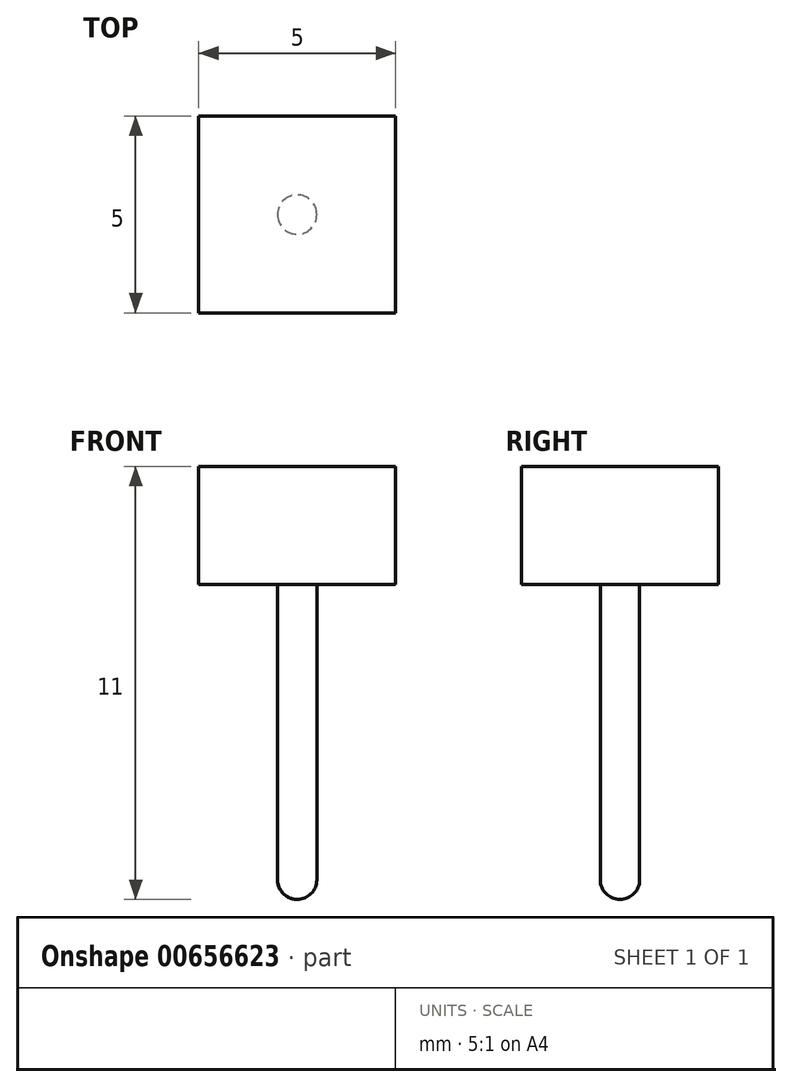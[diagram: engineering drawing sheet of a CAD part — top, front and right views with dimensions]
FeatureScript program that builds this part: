
annotation { "Feature Type Name" : "Feature", "Feature Type Description" : "" }
export const myFeature = defineFeature(function(context is Context, id is Id, definition is map)
    precondition{}
    {
        {
            var Q0;
            Q0=qCreatedBy(makeId("Top.planeOp"),FACE);
            var sketch = newSketch(context, id + "F0", { "sketchPlane" : qUnion([Q0])});
            skLineSegment(sketch, "E0.bottom", {"start": v(2.5, -2.5) * mm, "end": v(-2.5, -2.5) * mm});
            skLineSegment(sketch, "E0.top", {"start": v(2.5, 2.5) * mm, "end": v(-2.5, 2.5) * mm});
            skLineSegment(sketch, "E0.left", {"start": v(2.5, -2.5) * mm, "end": v(2.5, 2.5) * mm});
            skLineSegment(sketch, "E0.right", {"start": v(-2.5, -2.5) * mm, "end": v(-2.5, 2.5) * mm});
            skPoint(sketch, "E0.middle", {"position": v(0, 0) * mm});
            skSolve(sketch);
        }
        {
            var Q0;
            Q0 = qSketchRegion(id + "F0", true);
            extrude(context, id + "F1", {"entities" : qUnion([Q0]), "depth" : 3 * mm, "offsetDistance" : 25 * mm});
        }
        {
            var Q0;
            Q0=makeQuery(id+"F1.opExtrude","CAP_FACE",FACE,{"disambiguationData":[OSD([sQuery(id+"F0.wireOp",EDGE,"E0.bottom"),sQuery(id+"F0.wireOp",EDGE,"E0.top"),sQuery(id+"F0.wireOp",EDGE,"E0.left"),sQuery(id+"F0.wireOp",EDGE,"E0.right")])],"isStart":true});
            var sketch = newSketch(context, id + "F2", { "sketchPlane" : qUnion([Q0])});
            skCircle(sketch, "E1", {"center": v(0, 0) * mm, "radius": 0.5 * mm});
            skSolve(sketch);
        }
        {
            var Q0;
            Q0 = qSketchRegion(id + "F2", true);
            extrude(context, id + "F3", {"entities" : qUnion([Q0]), "operationType" : NewBodyOperationType.ADD, "depth" : 8 * mm, "offsetDistance" : 25 * mm});
        }
        {
            var Q0;
            Q0=makeQuery(id+"F3.opExtrude","CAP_EDGE",EDGE,{"disambiguationData":[OSD([sQuery(id+"F2.wireOp",EDGE,"E1")])],"isStart":false});
            fillet(context, id + "F4", {"entities" : qUnion([Q0]), "radius" : 0.5 * mm, "tangentPropagation" : true, "allowEdgeOverflow" : false});
        }
    });
